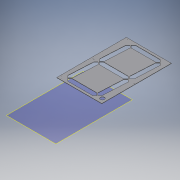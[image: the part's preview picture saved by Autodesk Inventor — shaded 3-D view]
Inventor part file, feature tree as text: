
AUTODESK INVENTOR PART (.ipt)
format: ipt  version: 2016 SP2 (Build 200236200, 236)  size: 174,592 bytes
history: native  units: mm
features: reference x49, extrude x2, sketch x2, plane x1
ambient origin geometry x8: Origin, YZ Plane, XZ Plane, XY Plane, X Axis, Y Axis, Z Axis, Center Point
bodies: Body1 (feature_tree)
feature tree (54):
  extrude  "Extrusion2"  Depth=4.5mm
  extrude  "Extrusion3"  Depth=0.6mm TaperAngle=0.0deg
  plane  "Arbeitsebene1"
  sketch  "Skizze1"  dims[d2=9.0mm d3=4.5mm]
  reference  "Referenz1"
  reference  "Referenz4"
  reference  "Referenz7"
  reference  "Referenz8"
  reference  "Referenz9"
  reference  "Referenz10"
  reference  "Referenz11"
  reference  "Referenz12"
  reference  "Referenz13"
  reference  "Referenz14"
  reference  "Referenz15"
  reference  "Referenz16"
  reference  "Referenz17"
  reference  "Referenz18"
  reference  "Referenz19"
  reference  "Referenz20"
  reference  "Referenz21"
  reference  "Referenz22"
  reference  "Referenz23"
  reference  "Referenz24"
  reference  "Referenz25"
  reference  "Referenz26"
  reference  "Referenz27"
  reference  "Referenz28"
  reference  "Referenz29"
  reference  "Referenz30"
  reference  "Referenz31"
  reference  "Referenz32"
  reference  "Referenz33"
  reference  "Referenz34"
  reference  "Referenz35"
  reference  "Referenz36"
  reference  "Referenz37"
  reference  "Referenz38"
  reference  "Referenz39"
  reference  "Referenz40"
  reference  "Referenz41"
  reference  "Referenz42"
  reference  "Referenz43"
  reference  "Referenz44"
  reference  "Referenz45"
  reference  "Referenz46"
  reference  "Referenz47"
  sketch  "Skizze2"  dims[d4=4.5mm d5=0.6mm d6=0.0mm d7=4.8mm d8=4.8mm d9=4.8mm d10=4.8mm d11=4.8mm d12=2.6mm d13=0.0mm d14=4.8mm]
  reference  "Referenz48"
  reference  "Referenz49"
  reference  "Referenz50"
  reference  "Referenz51"
  reference  "Referenz52"
  reference  "Referenz56"
